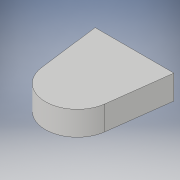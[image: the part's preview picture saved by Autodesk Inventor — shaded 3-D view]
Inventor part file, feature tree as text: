
AUTODESK INVENTOR PART (.ipt)
format: ipt  version: 2019 (Build 230136000, 136)  size: 96,256 bytes
history: native  units: mm
features: extrude x1, sketch x1
ambient origin geometry x8: Origin, YZ Plane, XZ Plane, XY Plane, X Axis, Y Axis, Z Axis, Center Point
bodies: Volumenkörper1 (feature_tree)
feature tree (2):
  extrude  "Extrusion1"  Depth=9.5mm
  sketch  "Skizze1"  dims[d0=25.0mm d1=32.0mm d2=39.0mm d3=35.0mm d4=9.5mm d5=0.0mm]
